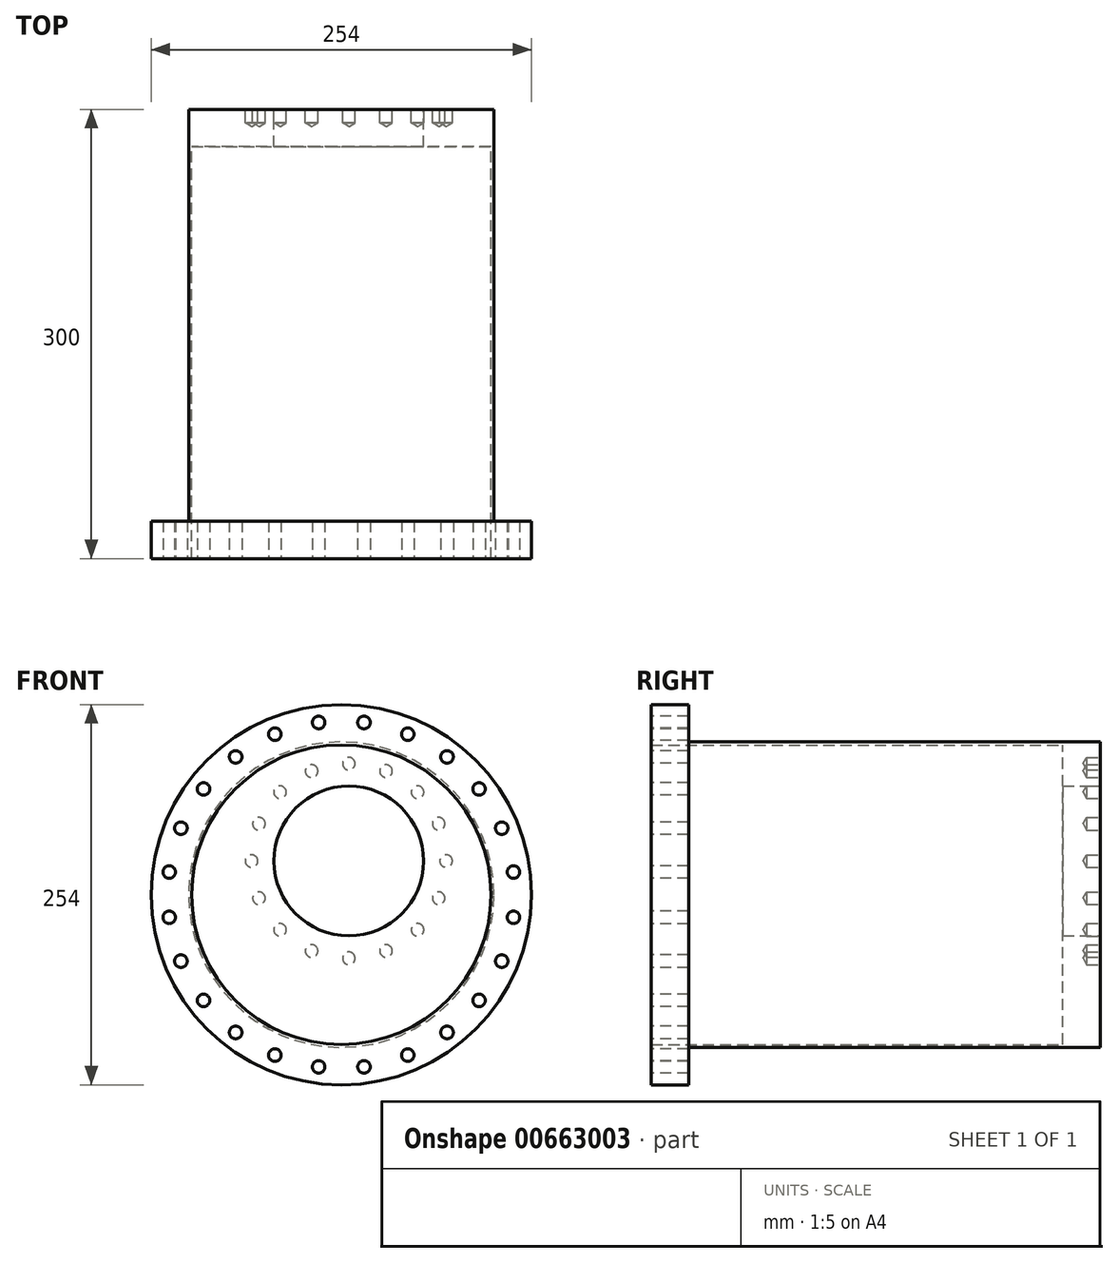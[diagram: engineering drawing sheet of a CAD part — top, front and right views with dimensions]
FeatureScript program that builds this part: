
annotation { "Feature Type Name" : "Feature", "Feature Type Description" : "" }
export const myFeature = defineFeature(function(context is Context, id is Id, definition is map)
    precondition{}
    {
        {
            var Q0;
            Q0=qCreatedBy(makeId("Front.planeOp"),FACE);
            var sketch = newSketch(context, id + "F0", { "sketchPlane" : qUnion([Q0])});
            skCircle(sketch, "E0", {"center": v(0, 0) * mm, "radius": 100 * mm});
            skCircle(sketch, "E1.0", {"center": v(0, 0) * mm, "radius": 102 * mm});
            skSolve(sketch);
        }
        {
            var Q0;
            Q0=makeQuery(id+"F0.imprint","IMPRINT",FACE,{"disambiguationData":[TD([[makeQuery(id+"F0.imprint","IMPRINT",EDGE,{"derivedFrom":sQuery(id+"F0.wireOp",EDGE,"E0")}),-1.0]])]});
            extrude(context, id + "F1", {"entities" : qUnion([Q0]), "depth" : (275 - 25) * mm, "offsetDistance" : 25 * mm});
        }
        {
            var Q0;
            Q0=makeQuery(id+"F1.opExtrude","CAP_FACE",FACE,{"disambiguationData":[OSD([sQuery(id+"F0.wireOp",EDGE,"E0"),sQuery(id+"F0.wireOp",EDGE,"E1.0")])],"isStart":false});
            var sketch = newSketch(context, id + "F2", { "sketchPlane" : qUnion([Q0])});
            skCircle(sketch, "E2", {"center": v(0, 0) * mm, "radius": 127 * mm});
            skSolve(sketch);
        }
        {
            var Q0;
            Q0=makeQuery(id+"F2.imprint","IMPRINT",FACE,{"disambiguationData":[TD([[makeQuery(id+"F2.imprint","IMPRINT",EDGE,{"derivedFrom":makeQuery(id+"F1.opExtrude","CAP_EDGE",EDGE,{"disambiguationData":[OSD([sQuery(id+"F0.wireOp",EDGE,"E0")])],"isStart":false})}),-1.0]])]});
            var Q1;
            Q1=makeQuery(id+"F2.imprint","IMPRINT",FACE,{"disambiguationData":[TD([[makeQuery(id+"F2.imprint","IMPRINT",EDGE,{"derivedFrom":sQuery(id+"F2.wireOp",EDGE,"E2")}),1.0]])]});
            extrude(context, id + "F3", {"entities" : qUnion([Q0, Q1]), "operationType" : NewBodyOperationType.ADD, "depth" : 25 * mm, "offsetDistance" : 25 * mm});
        }
        {
            var Q0;
            Q0=makeQuery(id+"F1.opExtrude","CAP_FACE",FACE,{"disambiguationData":[OSD([sQuery(id+"F0.wireOp",EDGE,"E0"),sQuery(id+"F0.wireOp",EDGE,"E1.0")])],"isStart":true});
            var sketch = newSketch(context, id + "F4", { "sketchPlane" : qUnion([Q0])});
            skCircle(sketch, "E3", {"center": v(0, 0) * mm, "radius": 102 * mm});
            skSolve(sketch);
        }
        {
            var Q0;
            Q0=makeQuery(id+"F4.imprint","IMPRINT",FACE,{"disambiguationData":[TD([[makeQuery(id+"F4.imprint","IMPRINT",EDGE,{"derivedFrom":makeQuery(id+"F1.opExtrude","CAP_EDGE",EDGE,{"disambiguationData":[OSD([sQuery(id+"F0.wireOp",EDGE,"E0")])],"isStart":true})}),-1.0]])]});
            var Q1;
            Q1=makeQuery(id+"F4.imprint","IMPRINT",FACE,{"disambiguationData":[TD([[makeQuery(id+"F4.imprint","IMPRINT",EDGE,{"derivedFrom":sQuery(id+"F4.wireOp",EDGE,"E3")}),-1.0]])]});
            extrude(context, id + "F5", {"entities" : qUnion([Q0, Q1]), "operationType" : NewBodyOperationType.ADD, "depth" : 25 * mm, "offsetDistance" : 25 * mm});
        }
        {
            var Q0;
            Q0=makeQuery(id+"F3.opExtrude","CAP_FACE",FACE,{"disambiguationData":[OSD([sQuery(id+"F0.wireOp",EDGE,"E0"),sQuery(id+"F2.wireOp",EDGE,"E2")])],"isStart":false});
            var sketch = newSketch(context, id + "F6", { "sketchPlane" : qUnion([Q0])});
            skCircle(sketch, "E4", {"center": v(0, 0) * mm, "radius": 116 * mm, "construction": true});
            skPoint(sketch, "E5", {"position": v(15.14, 115) * mm});
            skLineSegment(sketch, "E6", {"start": v(0, 0) * mm, "end": v(15.14, 115) * mm, "construction": true});
            skPoint(sketch, "E7.1.0", {"position": v(-15.14, 115) * mm});
            skPoint(sketch, "E7.2.0", {"position": v(-44.4, 107.17) * mm});
            skPoint(sketch, "E7.3.0", {"position": v(-70.62, 92.03) * mm});
            skPoint(sketch, "E7.4.0", {"position": v(-92.03, 70.62) * mm});
            skPoint(sketch, "E7.5.0", {"position": v(-107.17, 44.4) * mm});
            skPoint(sketch, "E7.6.0", {"position": v(-115, 15.14) * mm});
            skPoint(sketch, "E7.7.0", {"position": v(-115, -15.14) * mm});
            skPoint(sketch, "E7.8.0", {"position": v(-107.17, -44.4) * mm});
            skPoint(sketch, "E7.9.0", {"position": v(-92.03, -70.62) * mm});
            skPoint(sketch, "E7.10.0", {"position": v(-70.62, -92.03) * mm});
            skPoint(sketch, "E7.11.0", {"position": v(-44.4, -107.17) * mm});
            skPoint(sketch, "E7.12.0", {"position": v(-15.14, -115) * mm});
            skPoint(sketch, "E7.13.0", {"position": v(15.14, -115) * mm});
            skPoint(sketch, "E7.14.0", {"position": v(44.4, -107.17) * mm});
            skPoint(sketch, "E7.15.0", {"position": v(70.62, -92.03) * mm});
            skPoint(sketch, "E7.16.0", {"position": v(92.03, -70.62) * mm});
            skPoint(sketch, "E7.17.0", {"position": v(107.17, -44.4) * mm});
            skPoint(sketch, "E7.18.0", {"position": v(115, -15.14) * mm});
            skPoint(sketch, "E7.19.0", {"position": v(115, 15.14) * mm});
            skPoint(sketch, "E7.20.0", {"position": v(107.17, 44.4) * mm});
            skPoint(sketch, "E7.21.0", {"position": v(92.03, 70.62) * mm});
            skPoint(sketch, "E7.22.0", {"position": v(70.62, 92.03) * mm});
            skPoint(sketch, "E7.23.0", {"position": v(44.4, 107.17) * mm});
            skSolve(sketch);
        }
        {
            var Q0;
            Q0=sQuery(id+"F6.wireOp",VERTEX,"E5");
            var Q1;
            Q1=sQuery(id+"F6.wireOp",VERTEX,"E7.23.0");
            var Q2;
            Q2=sQuery(id+"F6.wireOp",VERTEX,"E7.22.0");
            var Q3;
            Q3=sQuery(id+"F6.wireOp",VERTEX,"E7.21.0");
            var Q4;
            Q4=sQuery(id+"F6.wireOp",VERTEX,"E7.20.0");
            var Q5;
            Q5=sQuery(id+"F6.wireOp",VERTEX,"E7.19.0");
            var Q6;
            Q6=sQuery(id+"F6.wireOp",VERTEX,"E7.18.0");
            var Q7;
            Q7=sQuery(id+"F6.wireOp",VERTEX,"E7.17.0");
            var Q8;
            Q8=sQuery(id+"F6.wireOp",VERTEX,"E7.16.0");
            var Q9;
            Q9=sQuery(id+"F6.wireOp",VERTEX,"E7.15.0");
            var Q10;
            Q10=sQuery(id+"F6.wireOp",VERTEX,"E7.14.0");
            var Q11;
            Q11=sQuery(id+"F6.wireOp",VERTEX,"E7.13.0");
            var Q12;
            Q12=sQuery(id+"F6.wireOp",VERTEX,"E7.12.0");
            var Q13;
            Q13=sQuery(id+"F6.wireOp",VERTEX,"E7.11.0");
            var Q14;
            Q14=sQuery(id+"F6.wireOp",VERTEX,"E7.10.0");
            var Q15;
            Q15=sQuery(id+"F6.wireOp",VERTEX,"E7.9.0");
            var Q16;
            Q16=sQuery(id+"F6.wireOp",VERTEX,"E7.8.0");
            var Q17;
            Q17=sQuery(id+"F6.wireOp",VERTEX,"E7.7.0");
            var Q18;
            Q18=sQuery(id+"F6.wireOp",VERTEX,"E7.6.0");
            var Q19;
            Q19=sQuery(id+"F6.wireOp",VERTEX,"E7.5.0");
            var Q20;
            Q20=sQuery(id+"F6.wireOp",VERTEX,"E7.4.0");
            var Q21;
            Q21=sQuery(id+"F6.wireOp",VERTEX,"E7.3.0");
            var Q22;
            Q22=sQuery(id+"F6.wireOp",VERTEX,"E7.2.0");
            var Q23;
            Q23=sQuery(id+"F6.wireOp",VERTEX,"E7.1.0");
            var Q24;
            Q24=makeQuery(id+"F1.opExtrude","SWEPT_BODY",BODY,{"disambiguationData":[OSD([sQuery(id+"F0.wireOp",EDGE,"E0"),sQuery(id+"F0.wireOp",EDGE,"E1.0")])]});
            hole(context, id + "F7", {"style" : HoleStyle.SIMPLE, "endStyle" : HoleEndStyle.THROUGH, "standardTappedOrClearance" : lookupTablePath({ "fit" : "Close", "standard" : "ISO", "size" : "M8", "type" : "Clearance" }), "standardBlindInLast" : lookupTablePath({ "fit" : "Close", "standard" : "ISO", "engagement" : "75%", "pitch" : "1.25 mm", "size" : "M8", "type" : "Clearance & tapped" }), "holeDiameter" : 8.4 * mm, "majorDiameter" : 5 * mm, "isTappedThrough" : true, "tappedDepth" : 12 * mm, "tapClearance" : 3, "locations" : qUnion([Q0, Q1, Q2, Q3, Q4, Q5, Q6, Q7, Q8, Q9, Q10, Q11, Q12, Q13, Q14, Q15, Q16, Q17, Q18, Q19, Q20, Q21, Q22, Q23]), "scope" : qUnion([Q24])});
        }
        {
            var Q0;
            Q0=makeQuery(id+"F5.opExtrude","CAP_FACE",FACE,{"disambiguationData":[OSD([sQuery(id+"F4.wireOp",EDGE,"E3")])],"isStart":false});
            var sketch = newSketch(context, id + "F8", { "sketchPlane" : qUnion([Q0])});
            skCircle(sketch, "E8", {"center": v(-5, 22.5) * mm, "radius": 50 * mm});
            skLineSegment(sketch, "E9", {"start": v(0, 0) * mm, "end": v(-5, 22.5) * mm, "construction": true});
            skCircle(sketch, "E10", {"center": v(-5, 22.5) * mm, "radius": 65 * mm, "construction": true});
            skPoint(sketch, "E11", {"position": v(-5, 87.5) * mm});
            skPoint(sketch, "E12.1.0", {"position": v(-29.87, 82.55) * mm});
            skPoint(sketch, "E12.2.0", {"position": v(-50.96, 68.46) * mm});
            skPoint(sketch, "E12.3.0", {"position": v(-65.05, 47.37) * mm});
            skPoint(sketch, "E12.4.0", {"position": v(-70, 22.5) * mm});
            skPoint(sketch, "E12.5.0", {"position": v(-65.05, -2.37) * mm});
            skPoint(sketch, "E12.6.0", {"position": v(-50.96, -23.46) * mm});
            skPoint(sketch, "E12.7.0", {"position": v(-29.87, -37.55) * mm});
            skPoint(sketch, "E13.0.8.0", {"position": v(-5, -42.5) * mm});
            skPoint(sketch, "E13.0.9.0", {"position": v(19.87, -37.55) * mm});
            skPoint(sketch, "E13.0.10.0", {"position": v(40.96, -23.46) * mm});
            skPoint(sketch, "E13.0.11.0", {"position": v(55.05, -2.37) * mm});
            skPoint(sketch, "E13.0.12.0", {"position": v(60, 22.5) * mm});
            skPoint(sketch, "E13.0.13.0", {"position": v(55.05, 47.37) * mm});
            skPoint(sketch, "E13.0.14.0", {"position": v(40.96, 68.46) * mm});
            skPoint(sketch, "E13.0.15.0", {"position": v(19.87, 82.55) * mm});
            skSolve(sketch);
        }
        {
            var Q0;
            Q0=makeQuery(id+"F8.imprint","IMPRINT",FACE,{"disambiguationData":[TD([[makeQuery(id+"F8.imprint","IMPRINT",EDGE,{"derivedFrom":sQuery(id+"F8.wireOp",EDGE,"E8")}),1.0]])]});
            extrude(context, id + "F9", {"entities" : qUnion([Q0]), "operationType" : NewBodyOperationType.REMOVE, "endBound" : BoundingType.THROUGH_ALL, "oppositeDirection" : true, "depth" : 25 * mm, "offsetDistance" : 25 * mm});
        }
        {
            var Q0;
            Q0=sQuery(id+"F8.wireOp",VERTEX,"E11");
            var Q1;
            Q1=sQuery(id+"F8.wireOp",VERTEX,"E12.7.0");
            var Q2;
            Q2=sQuery(id+"F8.wireOp",VERTEX,"E12.6.0");
            var Q3;
            Q3=sQuery(id+"F8.wireOp",VERTEX,"E12.5.0");
            var Q4;
            Q4=sQuery(id+"F8.wireOp",VERTEX,"E12.4.0");
            var Q5;
            Q5=sQuery(id+"F8.wireOp",VERTEX,"E12.3.0");
            var Q6;
            Q6=sQuery(id+"F8.wireOp",VERTEX,"E12.2.0");
            var Q7;
            Q7=sQuery(id+"F8.wireOp",VERTEX,"E12.1.0");
            var Q8;
            Q8=sQuery(id+"F8.wireOp",VERTEX,"E13.0.15.0");
            var Q9;
            Q9=sQuery(id+"F8.wireOp",VERTEX,"E13.0.14.0");
            var Q10;
            Q10=sQuery(id+"F8.wireOp",VERTEX,"E13.0.13.0");
            var Q11;
            Q11=sQuery(id+"F8.wireOp",VERTEX,"E13.0.12.0");
            var Q12;
            Q12=sQuery(id+"F8.wireOp",VERTEX,"E13.0.11.0");
            var Q13;
            Q13=sQuery(id+"F8.wireOp",VERTEX,"E13.0.10.0");
            var Q14;
            Q14=sQuery(id+"F8.wireOp",VERTEX,"E13.0.9.0");
            var Q15;
            Q15=sQuery(id+"F8.wireOp",VERTEX,"E13.0.8.0");
            var Q16;
            Q16=makeQuery(id+"F1.opExtrude","SWEPT_BODY",BODY,{"disambiguationData":[OSD([sQuery(id+"F0.wireOp",EDGE,"E0"),sQuery(id+"F0.wireOp",EDGE,"E1.0")])]});
            hole(context, id + "F10", {"style" : HoleStyle.SIMPLE, "endStyle" : HoleEndStyle.BLIND, "standardTappedOrClearance" : lookupTablePath({ "fit" : "Close", "standard" : "ISO", "size" : "M8", "type" : "Clearance" }), "standardBlindInLast" : lookupTablePath({ "fit" : "Close", "standard" : "ISO", "engagement" : "75%", "pitch" : "1.25 mm", "size" : "M8", "type" : "Clearance & tapped" }), "holeDiameter" : 8.4 * mm, "majorDiameter" : 5 * mm, "holeDepth" : 9 * mm, "isTappedThrough" : true, "tappedDepth" : 12 * mm, "tapClearance" : 3, "locations" : qUnion([Q0, Q1, Q2, Q3, Q4, Q5, Q6, Q7, Q8, Q9, Q10, Q11, Q12, Q13, Q14, Q15]), "scope" : qUnion([Q16])});
        }
    });
